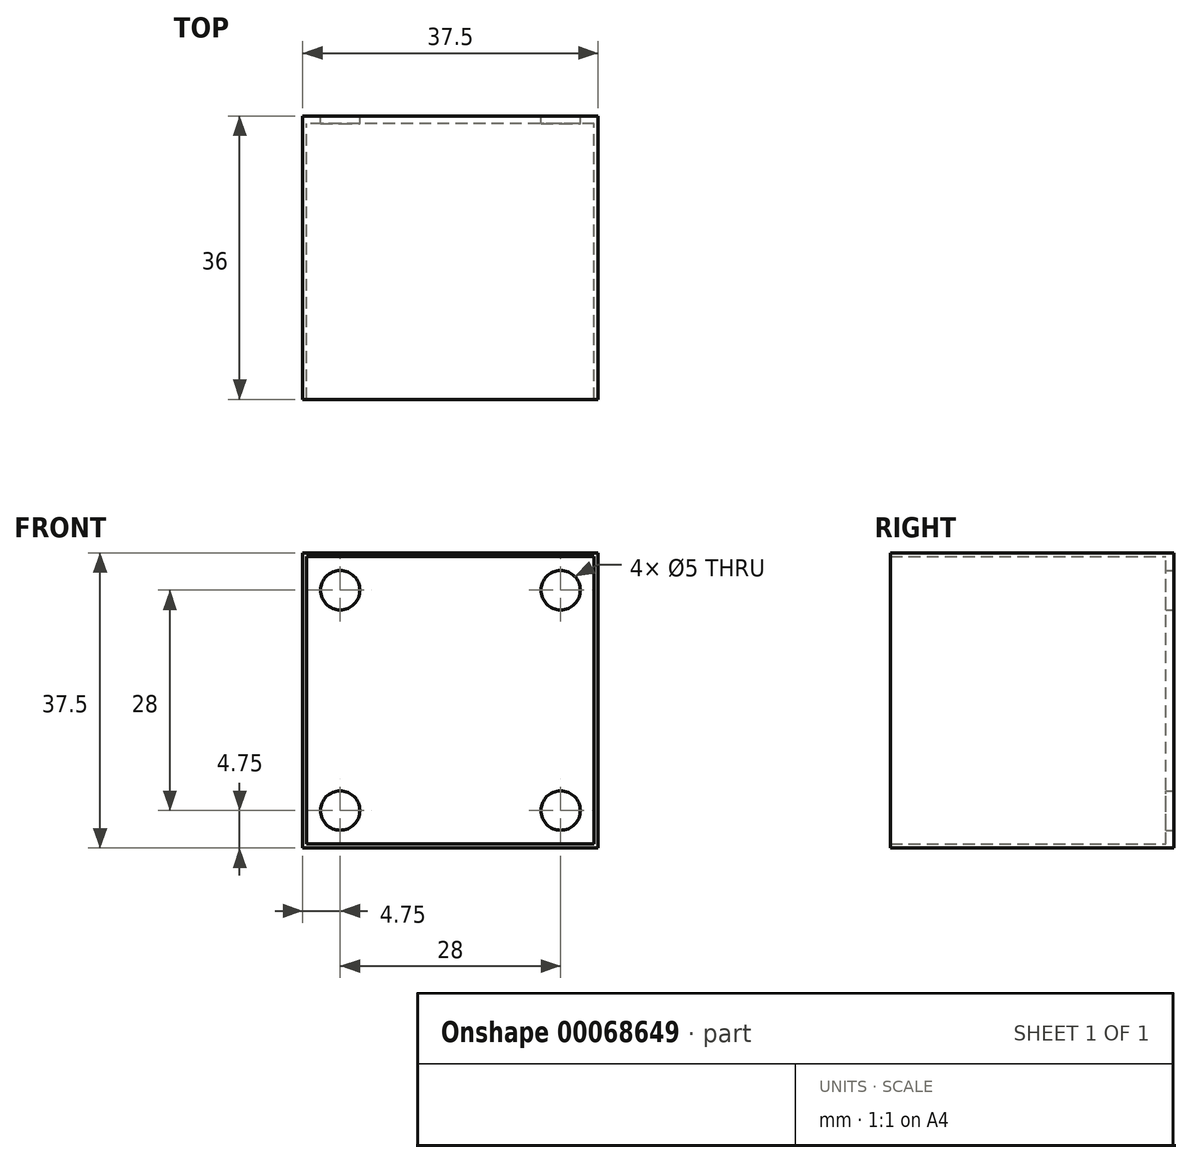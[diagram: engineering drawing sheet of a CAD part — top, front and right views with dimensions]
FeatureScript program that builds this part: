
annotation { "Feature Type Name" : "Feature", "Feature Type Description" : "" }
export const myFeature = defineFeature(function(context is Context, id is Id, definition is map)
    precondition{}
    {
        {
            var Q0;
            Q0=qCreatedBy(makeId("Front.planeOp"),FACE);
            var sketch = newSketch(context, id + "F0", { "sketchPlane" : qUnion([Q0])});
            skLineSegment(sketch, "E0.bottom", {"start": v(18, -18) * mm, "end": v(-18, -18) * mm});
            skLineSegment(sketch, "E0.top", {"start": v(18, 18) * mm, "end": v(-18, 18) * mm});
            skLineSegment(sketch, "E0.left", {"start": v(18, -18) * mm, "end": v(18, 18) * mm});
            skLineSegment(sketch, "E0.right", {"start": v(-18, -18) * mm, "end": v(-18, 18) * mm});
            skPoint(sketch, "E0.middle", {"position": v(0, 0) * mm});
            skLineSegment(sketch, "E1", {"start": v(-14, 18) * mm, "end": v(-14, -18) * mm, "construction": true});
            skLineSegment(sketch, "E2", {"start": v(-14, 18) * mm, "end": v(-18, 18) * mm, "construction": true});
            skLineSegment(sketch, "E3", {"start": v(-18, 14) * mm, "end": v(18, 14) * mm, "construction": true});
            skLineSegment(sketch, "E4", {"start": v(-14, 18) * mm, "end": v(-14, 14) * mm, "construction": true});
            skLineSegment(sketch, "E5", {"start": v(14, 18) * mm, "end": v(14, -18) * mm, "construction": true});
            skLineSegment(sketch, "E6", {"start": v(18, -14) * mm, "end": v(-18, -14) * mm, "construction": true});
            skLineSegment(sketch, "E7", {"start": v(18, 14) * mm, "end": v(14, 14) * mm, "construction": true});
            skLineSegment(sketch, "E8", {"start": v(14, -18) * mm, "end": v(14, -14) * mm, "construction": true});
            skCircle(sketch, "E9", {"center": v(-14, 14) * mm, "radius": 2.5 * mm});
            skCircle(sketch, "E10", {"center": v(14, 14) * mm, "radius": 2.5 * mm});
            skCircle(sketch, "E11", {"center": v(14, -14) * mm, "radius": 2.5 * mm});
            skLineSegment(sketch, "E12", {"start": v(-18, -14) * mm, "end": v(-14, -14) * mm});
            skCircle(sketch, "E13", {"center": v(-14, -14) * mm, "radius": 2.5 * mm});
            skLineSegment(sketch, "E14.bottom", {"start": v(18.25, -18.25) * mm, "end": v(-18.25, -18.25) * mm});
            skLineSegment(sketch, "E14.top", {"start": v(18.25, 18.25) * mm, "end": v(-18.25, 18.25) * mm});
            skLineSegment(sketch, "E14.left", {"start": v(18.25, -18.25) * mm, "end": v(18.25, 18.25) * mm});
            skLineSegment(sketch, "E14.right", {"start": v(-18.25, -18.25) * mm, "end": v(-18.25, 18.25) * mm});
            skLineSegment(sketch, "E15.bottom", {"start": v(-18.75, -18.75) * mm, "end": v(18.75, -18.75) * mm});
            skLineSegment(sketch, "E15.top", {"start": v(-18.75, 18.75) * mm, "end": v(18.75, 18.75) * mm});
            skLineSegment(sketch, "E15.left", {"start": v(-18.75, -18.75) * mm, "end": v(-18.75, 18.75) * mm});
            skLineSegment(sketch, "E15.right", {"start": v(18.75, -18.75) * mm, "end": v(18.75, 18.75) * mm});
            skSolve(sketch);
        }
        {
            var Q0;
            Q0=makeQuery(id+"F0.imprint","IMPRINT",FACE,{"disambiguationData":[TD([[makeQuery(id+"F0.imprint","IMPRINT",EDGE,{"derivedFrom":sQuery(id+"F0.wireOp",EDGE,"E14.bottom")}),1.0]])]});
            extrude(context, id + "F1", {"entities" : qUnion([Q0]), "depth" : 36 * mm});
        }
        {
            var Q0;
            {var subQ1=sQuery(id+"F0.wireOp",EDGE,"E0.bottom");Q0=makeQuery(id+"F0.imprint","IMPRINT",FACE,{"disambiguationData":[TD([[makeQuery(id+"F0.imprint","IMPRINT",EDGE,{"derivedFrom":subQ1}),1.0]])]});}
            var Q1;
            {var subQ1=sQuery(id+"F0.wireOp",EDGE,"E0.bottom");Q1=makeQuery(id+"F0.imprint","IMPRINT",FACE,{"disambiguationData":[TD([[makeQuery(id+"F0.imprint","IMPRINT",EDGE,{"derivedFrom":subQ1}),-1.0]])]});}
            extrude(context, id + "F2", {"entities" : qUnion([Q0, Q1]), "operationType" : NewBodyOperationType.ADD, "depth" : 1 * mm});
        }
    });
